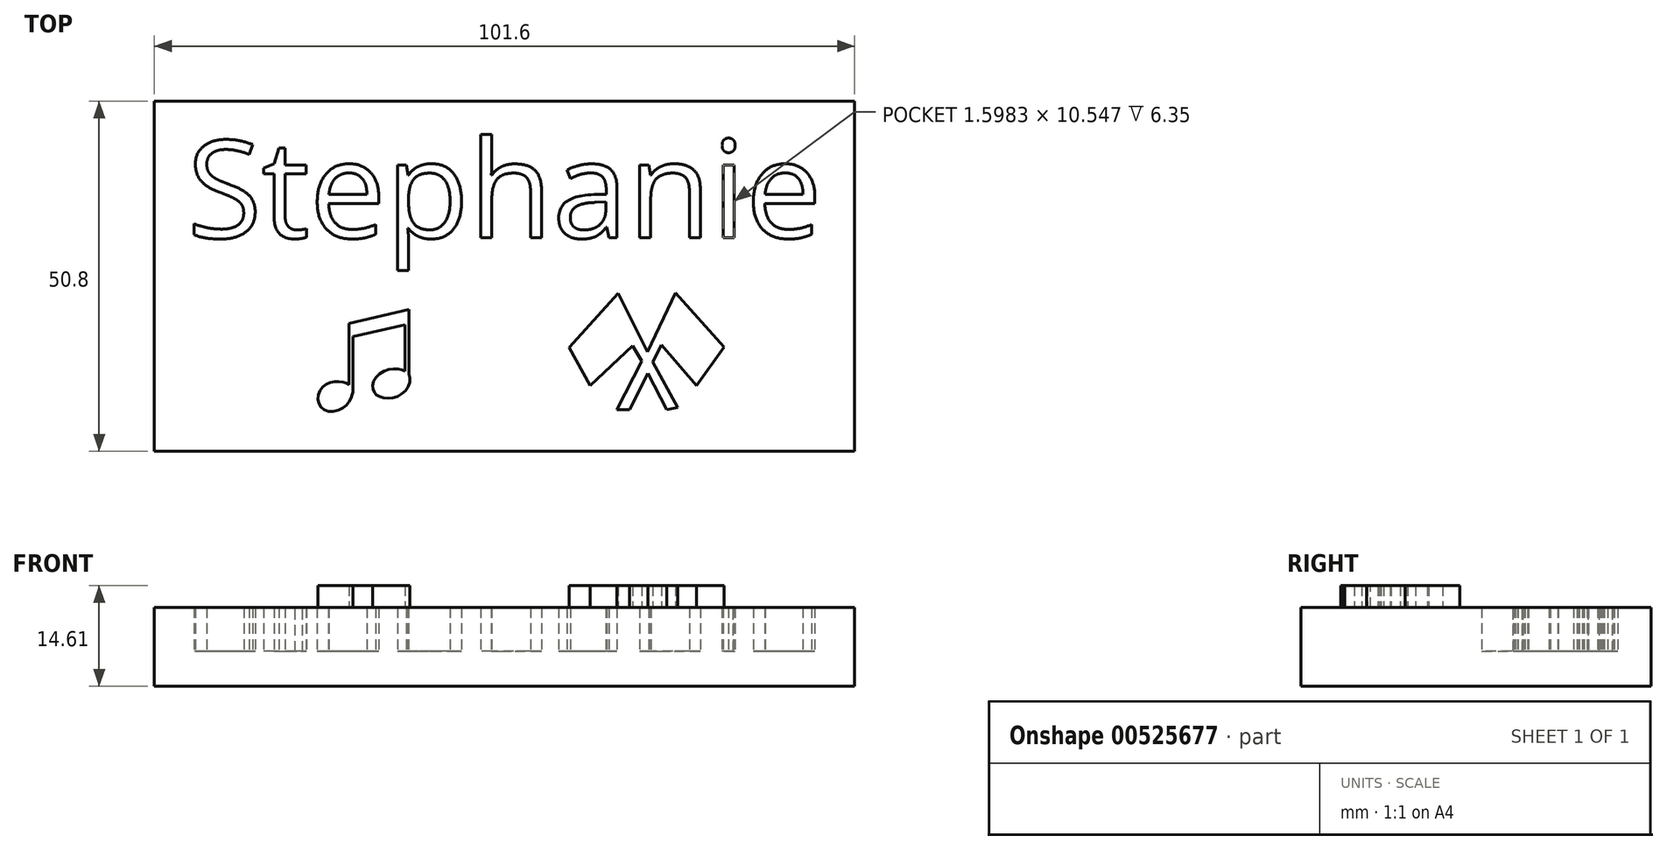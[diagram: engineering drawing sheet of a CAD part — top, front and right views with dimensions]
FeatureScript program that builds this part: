
annotation { "Feature Type Name" : "Feature", "Feature Type Description" : "" }
export const myFeature = defineFeature(function(context is Context, id is Id, definition is map)
    precondition{}
    {
        {
            var Q0;
            Q0=qCreatedBy(makeId("Top.planeOp"),FACE);
            var sketch = newSketch(context, id + "F0", { "sketchPlane" : qUnion([Q0])});
            skLineSegment(sketch, "E0.bottom", {"start": v(50.8, 25.4) * mm, "end": v(-50.8, 25.4) * mm});
            skLineSegment(sketch, "E0.top", {"start": v(50.8, -25.4) * mm, "end": v(-50.8, -25.4) * mm});
            skLineSegment(sketch, "E0.left", {"start": v(50.8, 25.4) * mm, "end": v(50.8, -25.4) * mm});
            skLineSegment(sketch, "E0.right", {"start": v(-50.8, 25.4) * mm, "end": v(-50.8, -25.4) * mm});
            skPoint(sketch, "E0.middle", {"position": v(0, 0) * mm});
            skSolve(sketch);
        }
        {
            var Q0;
            Q0=makeQuery(id+"F0.imprint","IMPRINT",FACE,{"disambiguationData":[TD([[makeQuery(id+"F0.imprint","IMPRINT",EDGE,{"derivedFrom":sQuery(id+"F0.wireOp",EDGE,"E0.bottom")}),1.0]])]});
            var Q1;
            Q1 = qSketchRegion(id + "F2", true);
            extrude(context, id + "F1", {"entities" : qUnion([Q0, Q1]), "depth" : 5.08 * mm, "offsetDistance" : 25.4 * mm});
        }
        {
            var Q0;
            Q0=makeQuery(id+"F1.opExtrude","CAP_FACE",FACE,{"disambiguationData":[OSD([sQuery(id+"F0.wireOp",EDGE,"E0.bottom"),sQuery(id+"F0.wireOp",EDGE,"E0.top"),sQuery(id+"F0.wireOp",EDGE,"E0.left"),sQuery(id+"F0.wireOp",EDGE,"E0.right")])],"isStart":false});
            var sketch = newSketch(context, id + "F2", { "sketchPlane" : qUnion([Q0])});
            skLineSegment(sketch, "E1.bottom", {"start": v(50.8, -25.4) * mm, "end": v(-50.8, -25.4) * mm});
            skLineSegment(sketch, "E1.top", {"start": v(50.8, 25.4) * mm, "end": v(-50.8, 25.4) * mm});
            skLineSegment(sketch, "E1.left", {"start": v(50.8, -25.4) * mm, "end": v(50.8, 25.4) * mm});
            skLineSegment(sketch, "E1.right", {"start": v(-50.8, -25.4) * mm, "end": v(-50.8, 25.4) * mm});
            skPoint(sketch, "E1.middle", {"position": v(0, 0) * mm});
            skText(sketch, "E2", { "text": "Stephanie", "fontName": "OpenSans-Regular.ttf"});
            const initialGuessF2  = {"E2": [-0.04605, 0.00558, 1, 0, 0.01419]};
            skSetInitialGuess(sketch, initialGuessF2);
            skSolve(sketch);
        }
        {
            var Q0;
            Q0 = qSketchRegion(id + "F2", true);
            var Q1;
            Q1=makeQuery(id+"F2.imprint","IMPRINT",FACE,{"disambiguationData":[TD([[makeQuery(id+"F2.imprint","IMPRINT",EDGE,{"derivedFrom":sQuery(id+"F2.wireOp",EDGE,"E2.sketch_text.stroke-58")}),1.0]])]});
            var Q2;
            Q2=makeQuery(id+"F2.imprint","IMPRINT",FACE,{"disambiguationData":[TD([[makeQuery(id+"F2.imprint","IMPRINT",EDGE,{"derivedFrom":sQuery(id+"F2.wireOp",EDGE,"E2.sketch_text.stroke-79")}),1.0]])]});
            var Q3;
            Q3=makeQuery(id+"F2.imprint","IMPRINT",FACE,{"disambiguationData":[TD([[makeQuery(id+"F2.imprint","IMPRINT",EDGE,{"derivedFrom":sQuery(id+"F2.wireOp",EDGE,"E2.sketch_text.stroke-125")}),1.0]])]});
            var Q4;
            Q4=makeQuery(id+"F2.imprint","IMPRINT",FACE,{"disambiguationData":[TD([[makeQuery(id+"F2.imprint","IMPRINT",EDGE,{"derivedFrom":sQuery(id+"F2.wireOp",EDGE,"E2.sketch_text.stroke-176")}),1.0]])]});
            extrude(context, id + "F3", {"entities" : qUnion([Q0, Q1, Q2, Q3, Q4]), "operationType" : NewBodyOperationType.ADD, "depth" : 6.35 * mm, "offsetDistance" : 25.4 * mm});
        }
        {
            var Q0;
            Q0=makeQuery(id+"F3.opExtrude","CAP_FACE",FACE,{"disambiguationData":[OSD([sQuery(id+"F2.wireOp",EDGE,"E1.bottom"),sQuery(id+"F2.wireOp",EDGE,"E1.top"),sQuery(id+"F2.wireOp",EDGE,"E1.left"),sQuery(id+"F2.wireOp",EDGE,"E1.right"),sQuery(id+"F2.wireOp",EDGE,"E2.sketch_text.stroke-0"),sQuery(id+"F2.wireOp",EDGE,"E2.sketch_text.stroke-1"),sQuery(id+"F2.wireOp",EDGE,"E2.sketch_text.stroke-2"),sQuery(id+"F2.wireOp",EDGE,"E2.sketch_text.stroke-3"),sQuery(id+"F2.wireOp",EDGE,"E2.sketch_text.stroke-4"),sQuery(id+"F2.wireOp",EDGE,"E2.sketch_text.stroke-5"),sQuery(id+"F2.wireOp",EDGE,"E2.sketch_text.stroke-6"),sQuery(id+"F2.wireOp",EDGE,"E2.sketch_text.stroke-7"),sQuery(id+"F2.wireOp",EDGE,"E2.sketch_text.stroke-8"),sQuery(id+"F2.wireOp",EDGE,"E2.sketch_text.stroke-9"),sQuery(id+"F2.wireOp",EDGE,"E2.sketch_text.stroke-10"),sQuery(id+"F2.wireOp",EDGE,"E2.sketch_text.stroke-11"),sQuery(id+"F2.wireOp",EDGE,"E2.sketch_text.stroke-12"),sQuery(id+"F2.wireOp",EDGE,"E2.sketch_text.stroke-13"),sQuery(id+"F2.wireOp",EDGE,"E2.sketch_text.stroke-14"),sQuery(id+"F2.wireOp",EDGE,"E2.sketch_text.stroke-15"),sQuery(id+"F2.wireOp",EDGE,"E2.sketch_text.stroke-16"),sQuery(id+"F2.wireOp",EDGE,"E2.sketch_text.stroke-17"),sQuery(id+"F2.wireOp",EDGE,"E2.sketch_text.stroke-18"),sQuery(id+"F2.wireOp",EDGE,"E2.sketch_text.stroke-19"),sQuery(id+"F2.wireOp",EDGE,"E2.sketch_text.stroke-20"),sQuery(id+"F2.wireOp",EDGE,"E2.sketch_text.stroke-21"),sQuery(id+"F2.wireOp",EDGE,"E2.sketch_text.stroke-22"),sQuery(id+"F2.wireOp",EDGE,"E2.sketch_text.stroke-23"),sQuery(id+"F2.wireOp",EDGE,"E2.sketch_text.stroke-24"),sQuery(id+"F2.wireOp",EDGE,"E2.sketch_text.stroke-25"),sQuery(id+"F2.wireOp",EDGE,"E2.sketch_text.stroke-26"),sQuery(id+"F2.wireOp",EDGE,"E2.sketch_text.stroke-27"),sQuery(id+"F2.wireOp",EDGE,"E2.sketch_text.stroke-28"),sQuery(id+"F2.wireOp",EDGE,"E2.sketch_text.stroke-29"),sQuery(id+"F2.wireOp",EDGE,"E2.sketch_text.stroke-30"),sQuery(id+"F2.wireOp",EDGE,"E2.sketch_text.stroke-31"),sQuery(id+"F2.wireOp",EDGE,"E2.sketch_text.stroke-32"),sQuery(id+"F2.wireOp",EDGE,"E2.sketch_text.stroke-33"),sQuery(id+"F2.wireOp",EDGE,"E2.sketch_text.stroke-34"),sQuery(id+"F2.wireOp",EDGE,"E2.sketch_text.stroke-35"),sQuery(id+"F2.wireOp",EDGE,"E2.sketch_text.stroke-36"),sQuery(id+"F2.wireOp",EDGE,"E2.sketch_text.stroke-37"),sQuery(id+"F2.wireOp",EDGE,"E2.sketch_text.stroke-38"),sQuery(id+"F2.wireOp",EDGE,"E2.sketch_text.stroke-39"),sQuery(id+"F2.wireOp",EDGE,"E2.sketch_text.stroke-40"),sQuery(id+"F2.wireOp",EDGE,"E2.sketch_text.stroke-41"),sQuery(id+"F2.wireOp",EDGE,"E2.sketch_text.stroke-42"),sQuery(id+"F2.wireOp",EDGE,"E2.sketch_text.stroke-43"),sQuery(id+"F2.wireOp",EDGE,"E2.sketch_text.stroke-44"),sQuery(id+"F2.wireOp",EDGE,"E2.sketch_text.stroke-45"),sQuery(id+"F2.wireOp",EDGE,"E2.sketch_text.stroke-46"),sQuery(id+"F2.wireOp",EDGE,"E2.sketch_text.stroke-47"),sQuery(id+"F2.wireOp",EDGE,"E2.sketch_text.stroke-48"),sQuery(id+"F2.wireOp",EDGE,"E2.sketch_text.stroke-49"),sQuery(id+"F2.wireOp",EDGE,"E2.sketch_text.stroke-50"),sQuery(id+"F2.wireOp",EDGE,"E2.sketch_text.stroke-51"),sQuery(id+"F2.wireOp",EDGE,"E2.sketch_text.stroke-52"),sQuery(id+"F2.wireOp",EDGE,"E2.sketch_text.stroke-53"),sQuery(id+"F2.wireOp",EDGE,"E2.sketch_text.stroke-54"),sQuery(id+"F2.wireOp",EDGE,"E2.sketch_text.stroke-55"),sQuery(id+"F2.wireOp",EDGE,"E2.sketch_text.stroke-56"),sQuery(id+"F2.wireOp",EDGE,"E2.sketch_text.stroke-57"),sQuery(id+"F2.wireOp",EDGE,"E2.sketch_text.stroke-63"),sQuery(id+"F2.wireOp",EDGE,"E2.sketch_text.stroke-64"),sQuery(id+"F2.wireOp",EDGE,"E2.sketch_text.stroke-65"),sQuery(id+"F2.wireOp",EDGE,"E2.sketch_text.stroke-66"),sQuery(id+"F2.wireOp",EDGE,"E2.sketch_text.stroke-67"),sQuery(id+"F2.wireOp",EDGE,"E2.sketch_text.stroke-68"),sQuery(id+"F2.wireOp",EDGE,"E2.sketch_text.stroke-69"),sQuery(id+"F2.wireOp",EDGE,"E2.sketch_text.stroke-70"),sQuery(id+"F2.wireOp",EDGE,"E2.sketch_text.stroke-71"),sQuery(id+"F2.wireOp",EDGE,"E2.sketch_text.stroke-72"),sQuery(id+"F2.wireOp",EDGE,"E2.sketch_text.stroke-73"),sQuery(id+"F2.wireOp",EDGE,"E2.sketch_text.stroke-74"),sQuery(id+"F2.wireOp",EDGE,"E2.sketch_text.stroke-75"),sQuery(id+"F2.wireOp",EDGE,"E2.sketch_text.stroke-76"),sQuery(id+"F2.wireOp",EDGE,"E2.sketch_text.stroke-77"),sQuery(id+"F2.wireOp",EDGE,"E2.sketch_text.stroke-78"),sQuery(id+"F2.wireOp",EDGE,"E2.sketch_text.stroke-88"),sQuery(id+"F2.wireOp",EDGE,"E2.sketch_text.stroke-89"),sQuery(id+"F2.wireOp",EDGE,"E2.sketch_text.stroke-90"),sQuery(id+"F2.wireOp",EDGE,"E2.sketch_text.stroke-91"),sQuery(id+"F2.wireOp",EDGE,"E2.sketch_text.stroke-92"),sQuery(id+"F2.wireOp",EDGE,"E2.sketch_text.stroke-93"),sQuery(id+"F2.wireOp",EDGE,"E2.sketch_text.stroke-94"),sQuery(id+"F2.wireOp",EDGE,"E2.sketch_text.stroke-95"),sQuery(id+"F2.wireOp",EDGE,"E2.sketch_text.stroke-96"),sQuery(id+"F2.wireOp",EDGE,"E2.sketch_text.stroke-97"),sQuery(id+"F2.wireOp",EDGE,"E2.sketch_text.stroke-98"),sQuery(id+"F2.wireOp",EDGE,"E2.sketch_text.stroke-99"),sQuery(id+"F2.wireOp",EDGE,"E2.sketch_text.stroke-100"),sQuery(id+"F2.wireOp",EDGE,"E2.sketch_text.stroke-101"),sQuery(id+"F2.wireOp",EDGE,"E2.sketch_text.stroke-102"),sQuery(id+"F2.wireOp",EDGE,"E2.sketch_text.stroke-103"),sQuery(id+"F2.wireOp",EDGE,"E2.sketch_text.stroke-104"),sQuery(id+"F2.wireOp",EDGE,"E2.sketch_text.stroke-105"),sQuery(id+"F2.wireOp",EDGE,"E2.sketch_text.stroke-106"),sQuery(id+"F2.wireOp",EDGE,"E2.sketch_text.stroke-107"),sQuery(id+"F2.wireOp",EDGE,"E2.sketch_text.stroke-108"),sQuery(id+"F2.wireOp",EDGE,"E2.sketch_text.stroke-109"),sQuery(id+"F2.wireOp",EDGE,"E2.sketch_text.stroke-110"),sQuery(id+"F2.wireOp",EDGE,"E2.sketch_text.stroke-111"),sQuery(id+"F2.wireOp",EDGE,"E2.sketch_text.stroke-112"),sQuery(id+"F2.wireOp",EDGE,"E2.sketch_text.stroke-113"),sQuery(id+"F2.wireOp",EDGE,"E2.sketch_text.stroke-114"),sQuery(id+"F2.wireOp",EDGE,"E2.sketch_text.stroke-115"),sQuery(id+"F2.wireOp",EDGE,"E2.sketch_text.stroke-116"),sQuery(id+"F2.wireOp",EDGE,"E2.sketch_text.stroke-117"),sQuery(id+"F2.wireOp",EDGE,"E2.sketch_text.stroke-118"),sQuery(id+"F2.wireOp",EDGE,"E2.sketch_text.stroke-119"),sQuery(id+"F2.wireOp",EDGE,"E2.sketch_text.stroke-120"),sQuery(id+"F2.wireOp",EDGE,"E2.sketch_text.stroke-121"),sQuery(id+"F2.wireOp",EDGE,"E2.sketch_text.stroke-122"),sQuery(id+"F2.wireOp",EDGE,"E2.sketch_text.stroke-123"),sQuery(id+"F2.wireOp",EDGE,"E2.sketch_text.stroke-124"),sQuery(id+"F2.wireOp",EDGE,"E2.sketch_text.stroke-133"),sQuery(id+"F2.wireOp",EDGE,"E2.sketch_text.stroke-134"),sQuery(id+"F2.wireOp",EDGE,"E2.sketch_text.stroke-135"),sQuery(id+"F2.wireOp",EDGE,"E2.sketch_text.stroke-136"),sQuery(id+"F2.wireOp",EDGE,"E2.sketch_text.stroke-137"),sQuery(id+"F2.wireOp",EDGE,"E2.sketch_text.stroke-138"),sQuery(id+"F2.wireOp",EDGE,"E2.sketch_text.stroke-139"),sQuery(id+"F2.wireOp",EDGE,"E2.sketch_text.stroke-140"),sQuery(id+"F2.wireOp",EDGE,"E2.sketch_text.stroke-141"),sQuery(id+"F2.wireOp",EDGE,"E2.sketch_text.stroke-142"),sQuery(id+"F2.wireOp",EDGE,"E2.sketch_text.stroke-143"),sQuery(id+"F2.wireOp",EDGE,"E2.sketch_text.stroke-144"),sQuery(id+"F2.wireOp",EDGE,"E2.sketch_text.stroke-145"),sQuery(id+"F2.wireOp",EDGE,"E2.sketch_text.stroke-146"),sQuery(id+"F2.wireOp",EDGE,"E2.sketch_text.stroke-147"),sQuery(id+"F2.wireOp",EDGE,"E2.sketch_text.stroke-148"),sQuery(id+"F2.wireOp",EDGE,"E2.sketch_text.stroke-149"),sQuery(id+"F2.wireOp",EDGE,"E2.sketch_text.stroke-150"),sQuery(id+"F2.wireOp",EDGE,"E2.sketch_text.stroke-151"),sQuery(id+"F2.wireOp",EDGE,"E2.sketch_text.stroke-152"),sQuery(id+"F2.wireOp",EDGE,"E2.sketch_text.stroke-153"),sQuery(id+"F2.wireOp",EDGE,"E2.sketch_text.stroke-154"),sQuery(id+"F2.wireOp",EDGE,"E2.sketch_text.stroke-155"),sQuery(id+"F2.wireOp",EDGE,"E2.sketch_text.stroke-156"),sQuery(id+"F2.wireOp",EDGE,"E2.sketch_text.stroke-157"),sQuery(id+"F2.wireOp",EDGE,"E2.sketch_text.stroke-158"),sQuery(id+"F2.wireOp",EDGE,"E2.sketch_text.stroke-159"),sQuery(id+"F2.wireOp",EDGE,"E2.sketch_text.stroke-160"),sQuery(id+"F2.wireOp",EDGE,"E2.sketch_text.stroke-161"),sQuery(id+"F2.wireOp",EDGE,"E2.sketch_text.stroke-162"),sQuery(id+"F2.wireOp",EDGE,"E2.sketch_text.stroke-163"),sQuery(id+"F2.wireOp",EDGE,"E2.sketch_text.stroke-164"),sQuery(id+"F2.wireOp",EDGE,"E2.sketch_text.stroke-165"),sQuery(id+"F2.wireOp",EDGE,"E2.sketch_text.stroke-166"),sQuery(id+"F2.wireOp",EDGE,"E2.sketch_text.stroke-167"),sQuery(id+"F2.wireOp",EDGE,"E2.sketch_text.stroke-168"),sQuery(id+"F2.wireOp",EDGE,"E2.sketch_text.stroke-169"),sQuery(id+"F2.wireOp",EDGE,"E2.sketch_text.stroke-170"),sQuery(id+"F2.wireOp",EDGE,"E2.sketch_text.stroke-171"),sQuery(id+"F2.wireOp",EDGE,"E2.sketch_text.stroke-172"),sQuery(id+"F2.wireOp",EDGE,"E2.sketch_text.stroke-173"),sQuery(id+"F2.wireOp",EDGE,"E2.sketch_text.stroke-174"),sQuery(id+"F2.wireOp",EDGE,"E2.sketch_text.stroke-175")])],"isStart":false});
            var sketch = newSketch(context, id + "F4", { "sketchPlane" : qUnion([Q0])});
            skLineSegment(sketch, "E3", {"start": v(-22.01, -16.56) * mm, "end": v(-22.01, -8.8) * mm});
            skLineSegment(sketch, "E4", {"start": v(-22.01, -8.8) * mm, "end": v(-14.4, -7.08) * mm});
            skLineSegment(sketch, "E5", {"start": v(-14.4, -7.08) * mm, "end": v(-14.4, -13.8) * mm});
            skLineSegment(sketch, "E6", {"start": v(-14.4, -13.8) * mm, "end": v(-13.85, -14.22) * mm});
            skLineSegment(sketch, "E7", {"start": v(-13.85, -14.22) * mm, "end": v(-13.85, -4.82) * mm});
            skLineSegment(sketch, "E8", {"start": v(-13.85, -4.82) * mm, "end": v(-22.56, -6.87) * mm});
            skLineSegment(sketch, "E9", {"start": v(-22.56, -6.87) * mm, "end": v(-22.56, -15.74) * mm});
            skLineSegment(sketch, "E10", {"start": v(-22.56, -15.74) * mm, "end": v(-22.01, -16.56) * mm});
            skFitSpline(sketch, "E11", {"points": [v(-22.01, -16.87) * mm, v(-22.38, -17.93) * mm, v(-23.7, -19.27) * mm, v(-25.9, -19.5) * mm, v(-26.99, -18.27) * mm, v(-26.75, -16.56) * mm, v(-25.33, -15.45) * mm, v(-23.62, -15.35) * mm, v(-22.56, -15.74) * mm, v(-22.01, -16.56) * mm, v(-22.01, -16.87) * mm]});
            skFitSpline(sketch, "E12", {"points": [v(-14.4, -13.8) * mm, v(-15.67, -13.45) * mm, v(-17.54, -13.8) * mm, v(-19.01, -15.32) * mm, v(-19.04, -16.56) * mm, v(-18.46, -17.32) * mm, v(-16.96, -17.7) * mm, v(-15.14, -17.24) * mm, v(-13.85, -15.74) * mm, v(-13.85, -14.22) * mm, v(-14.4, -13.8) * mm]});
            skSolve(sketch);
        }
        {
            var Q0;
            Q0=makeQuery(id+"F4.imprint","IMPRINT",FACE,{"disambiguationData":[TD([[makeQuery(id+"F4.imprint","IMPRINT",EDGE,{"derivedFrom":makeQuery(id+"F3.opExtrude","CAP_EDGE",EDGE,{"disambiguationData":[OSD([sQuery(id+"F2.wireOp",EDGE,"E1.bottom")])],"isStart":false})}),-1.0]])]});
            var sketch = newSketch(context, id + "F5", { "sketchPlane" : qUnion([Q0])});
            skLineSegment(sketch, "E13", {"start": v(25.15, -19.06) * mm, "end": v(21.54, -12.47) * mm});
            skLineSegment(sketch, "E14", {"start": v(21.54, -12.47) * mm, "end": v(22.77, -9.94) * mm});
            skLineSegment(sketch, "E15", {"start": v(22.77, -9.94) * mm, "end": v(27.83, -15.9) * mm});
            skLineSegment(sketch, "E16", {"start": v(27.83, -15.9) * mm, "end": v(31.85, -10.31) * mm});
            skLineSegment(sketch, "E17", {"start": v(31.85, -10.31) * mm, "end": v(24.81, -2.39) * mm});
            skLineSegment(sketch, "E18", {"start": v(24.81, -2.39) * mm, "end": v(20.76, -10.98) * mm});
            skLineSegment(sketch, "E19", {"start": v(20.76, -10.98) * mm, "end": v(16.48, -2.46) * mm});
            skLineSegment(sketch, "E20", {"start": v(16.48, -2.46) * mm, "end": v(9.4, -10.35) * mm});
            skLineSegment(sketch, "E21", {"start": v(9.4, -10.35) * mm, "end": v(12.42, -15.9) * mm});
            skLineSegment(sketch, "E22", {"start": v(12.42, -15.9) * mm, "end": v(18.56, -10.1) * mm});
            skLineSegment(sketch, "E23", {"start": v(18.56, -10.1) * mm, "end": v(19.9, -12.33) * mm});
            skLineSegment(sketch, "E24", {"start": v(19.9, -12.33) * mm, "end": v(16.33, -19.4) * mm});
            skLineSegment(sketch, "E25", {"start": v(16.33, -19.4) * mm, "end": v(18.11, -19.4) * mm});
            skLineSegment(sketch, "E26", {"start": v(18.11, -19.4) * mm, "end": v(20.8, -14.07) * mm});
            skLineSegment(sketch, "E27", {"start": v(20.8, -14.07) * mm, "end": v(23.51, -19.4) * mm});
            skLineSegment(sketch, "E28", {"start": v(23.51, -19.4) * mm, "end": v(25.15, -19.06) * mm});
            skSolve(sketch);
        }
        {
            var Q0;
            Q0 = qSketchRegion(id + "F5", true);
            extrude(context, id + "F6", {"entities" : qUnion([Q0]), "operationType" : NewBodyOperationType.ADD, "depth" : 3.17 * mm, "offsetDistance" : 25.4 * mm});
        }
        {
            var Q0;
            {var subQ0=sQuery(id+"F4.wireOp",EDGE,"E6");Q0=makeQuery(id+"F4.imprint","IMPRINT",FACE,{"disambiguationData":[TD([[makeQuery(id+"F4.imprint","IMPRINT",EDGE,{"derivedFrom":subQ0}),1.0]])]});}
            var Q1;
            {var subQ0=sQuery(id+"F4.wireOp",EDGE,"E10");Q1=makeQuery(id+"F4.imprint","IMPRINT",FACE,{"disambiguationData":[TD([[makeQuery(id+"F4.imprint","IMPRINT",EDGE,{"derivedFrom":subQ0}),1.0]])]});}
            var Q2;
            {var subQ0=sQuery(id+"F4.wireOp",EDGE,"E10");Q2=makeQuery(id+"F4.imprint","IMPRINT",FACE,{"disambiguationData":[TD([[makeQuery(id+"F4.imprint","IMPRINT",EDGE,{"derivedFrom":subQ0}),-1.0]])]});}
            var Q3;
            {var subQ2=sQuery(id+"F4.wireOp",EDGE,"E3");Q3=makeQuery(id+"F4.imprint","IMPRINT",FACE,{"disambiguationData":[TD([[makeQuery(id+"F4.imprint","IMPRINT",EDGE,{"derivedFrom":subQ2}),1.0]])]});}
            extrude(context, id + "F7", {"entities" : qUnion([Q0, Q1, Q2, Q3]), "operationType" : NewBodyOperationType.ADD, "depth" : 3.17 * mm, "offsetDistance" : 25.4 * mm});
        }
        {
            var Q0;
            Q0 = qSketchRegion(id + "F4", true);
            extrude(context, id + "F8", {"entities" : qUnion([Q0]), "operationType" : NewBodyOperationType.ADD, "depth" : 3.17 * mm, "offsetDistance" : 25.4 * mm});
        }
    });
